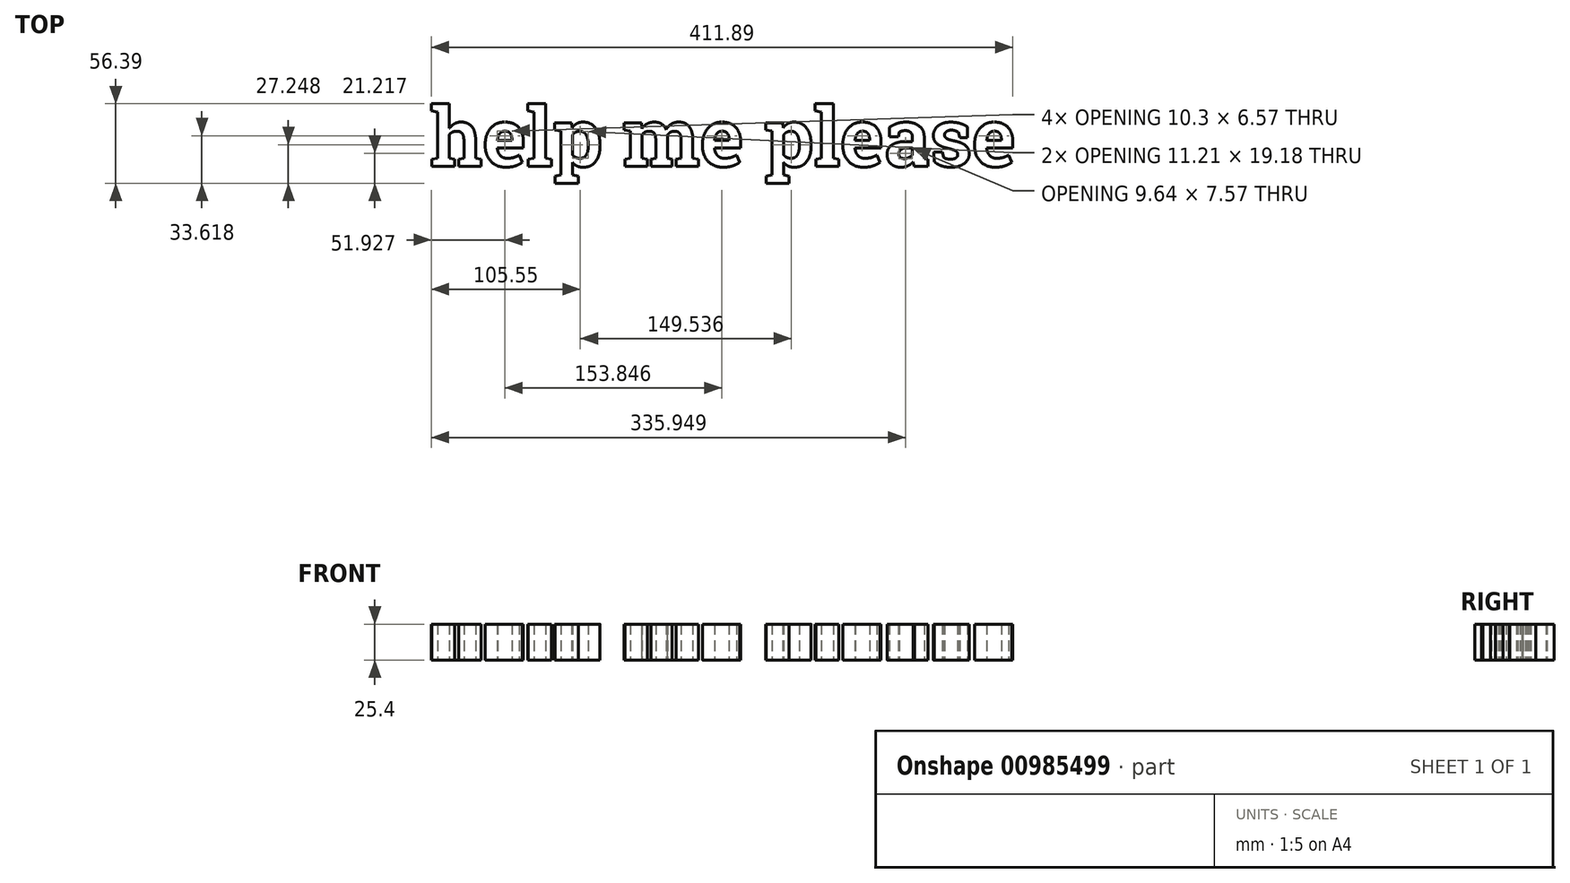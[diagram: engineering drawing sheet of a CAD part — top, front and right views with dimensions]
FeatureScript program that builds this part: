
annotation { "Feature Type Name" : "Feature", "Feature Type Description" : "" }
export const myFeature = defineFeature(function(context is Context, id is Id, definition is map)
    precondition{}
    {
        {
            var Q0;
            Q0=qCreatedBy(makeId("Top.planeOp"),FACE);
            var sketch = newSketch(context, id + "F0", { "sketchPlane" : qUnion([Q0])});
            skText(sketch, "E0", { "text": "help me please", "fontName": "RobotoSlab-Bold.ttf"});
            const initialGuessF0  = {"E0": [-0.07314, 0.0315, 1, 0, 0.04208]};
            skSetInitialGuess(sketch, initialGuessF0);
            skSolve(sketch);
        }
        {
            var Q0;
            Q0 = qSketchRegion(id + "F0", true);
            extrude(context, id + "F1", {"entities" : qUnion([Q0]), "depth" : 25.4 * mm, "offsetDistance" : 25.4 * mm});
        }
    });
